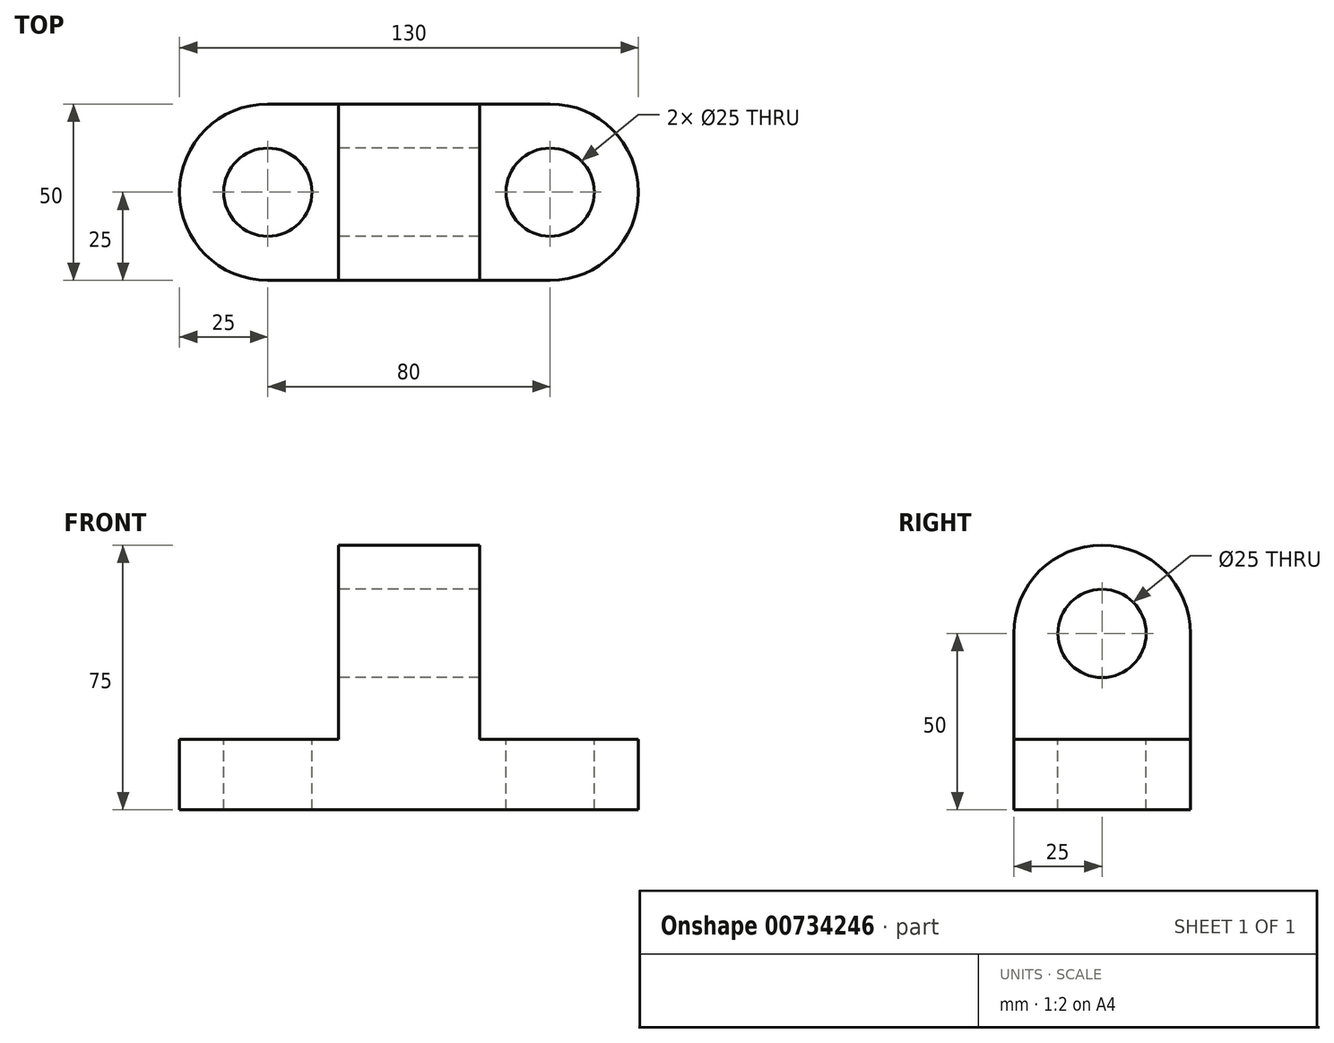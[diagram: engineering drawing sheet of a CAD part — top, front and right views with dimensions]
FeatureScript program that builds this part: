
annotation { "Feature Type Name" : "Feature", "Feature Type Description" : "" }
export const myFeature = defineFeature(function(context is Context, id is Id, definition is map)
    precondition{}
    {
        {
            var Q0;
            Q0=qCreatedBy(makeId("Top.planeOp"),FACE);
            var sketch = newSketch(context, id + "F0", { "sketchPlane" : qUnion([Q0])});
            skLineSegment(sketch, "E0", {"start": v(0, 50) * mm, "end": v(80, 50) * mm});
            skLineSegment(sketch, "E1", {"start": v(0, 0) * mm, "end": v(80, 0) * mm});
            skArc(sketch, "E2", {"start": v(80, 0) * mm, "mid": v(105, 25) * mm, "end": v(80, 50) * mm});
            skArc(sketch, "E3", {"start": v(0, 50) * mm, "mid": v(-25, 25) * mm, "end": v(0, 0) * mm});
            skSolve(sketch);
        }
        {
            var Q0;
            Q0=makeQuery(id+"F0.imprint","IMPRINT",FACE,{"disambiguationData":[TD([[makeQuery(id+"F0.imprint","IMPRINT",EDGE,{"derivedFrom":sQuery(id+"F0.wireOp",EDGE,"E0")}),-1.0]])]});
            extrude(context, id + "F1", {"entities" : qUnion([Q0]), "depth" : 20 * mm, "offsetDistance" : 25 * mm});
        }
        {
            var Q0;
            Q0=makeQuery(id+"F1.opExtrude","CAP_FACE",FACE,{"disambiguationData":[OSD([sQuery(id+"F0.wireOp",EDGE,"E0"),sQuery(id+"F0.wireOp",EDGE,"E1"),sQuery(id+"F0.wireOp",EDGE,"E2"),sQuery(id+"F0.wireOp",EDGE,"E3")])],"isStart":false});
            var sketch = newSketch(context, id + "F2", { "sketchPlane" : qUnion([Q0])});
            skLineSegment(sketch, "E4", {"start": v(20, 50) * mm, "end": v(20, 0) * mm});
            skLineSegment(sketch, "E5", {"start": v(60, 50) * mm, "end": v(60, 0) * mm});
            skSolve(sketch);
        }
        {
            var Q0;
            {var subQ0=sQuery(id+"F2.wireOp",EDGE,"E4");Q0=makeQuery(id+"F2.imprint","IMPRINT",FACE,{"disambiguationData":[TD([[makeQuery(id+"F2.imprint","IMPRINT",EDGE,{"derivedFrom":subQ0}),1.0]])]});}
            extrude(context, id + "F3", {"entities" : qUnion([Q0]), "operationType" : NewBodyOperationType.ADD, "depth" : 30 * mm, "offsetDistance" : 25 * mm});
        }
        {
            var Q0;
            Q0=makeQuery(id+"F3.opExtrude","SWEPT_FACE",FACE,{"disambiguationData":[OSD([sQuery(id+"F2.wireOp",EDGE,"E5")])]});
            var sketch = newSketch(context, id + "F4", { "sketchPlane" : qUnion([Q0])});
            skArc(sketch, "E6", {"start": v(50, 50) * mm, "mid": v(25, 75) * mm, "end": v(0, 50) * mm});
            skLineSegment(sketch, "E7.0", {"start": v(0, 20) * mm, "end": v(50, 20) * mm});
            skSolve(sketch);
        }
        {
            var Q0;
            Q0=makeQuery(id+"F4.imprint","IMPRINT",FACE,{"disambiguationData":[TD([[makeQuery(id+"F4.imprint","IMPRINT",EDGE,{"derivedFrom":sQuery(id+"F4.wireOp",EDGE,"E6")}),1.0]])]});
            var Q1;
            Q1=makeQuery(id+"F3.opExtrude","SWEPT_FACE",FACE,{"disambiguationData":[OSD([sQuery(id+"F2.wireOp",EDGE,"E4")])]});
            extrude(context, id + "F5", {"entities" : qUnion([Q0]), "operationType" : NewBodyOperationType.ADD, "endBound" : BoundingType.UP_TO_SURFACE, "oppositeDirection" : true, "depth" : 25 * mm, "endBoundEntityFace" : qUnion([Q1]), "offsetDistance" : 25 * mm});
        }
        {
            var Q0;
            {var subQ0=sQuery(id+"F2.wireOp",EDGE,"E4");Q0=makeQuery(id+"F5.boolean.opBoolean","MERGE",FACE,{"derivedFrom":[makeQuery(id+"F3.opExtrude","SWEPT_FACE",FACE,{"disambiguationData":[OSD([subQ0])]}),makeQuery(id+"F5.opExtrude","CAP_FACE",FACE,{"disambiguationData":[OSD([subQ0])],"isStart":false})]});}
            var sketch = newSketch(context, id + "F6", { "sketchPlane" : qUnion([Q0])});
            skCircle(sketch, "E8", {"center": v(-25, 50) * mm, "radius": 12.5 * mm});
            skSolve(sketch);
        }
        {
            var Q0;
            Q0=makeQuery(id+"F6.imprint","IMPRINT",FACE,{"disambiguationData":[TD([[makeQuery(id+"F6.imprint","IMPRINT",EDGE,{"derivedFrom":sQuery(id+"F6.wireOp",EDGE,"E8")}),1.0]])]});
            var Q1;
            {var subQ0=sQuery(id+"F2.wireOp",EDGE,"E5");Q1=makeQuery(id+"F5.boolean.opBoolean","MERGE",FACE,{"derivedFrom":[makeQuery(id+"F3.opExtrude","SWEPT_FACE",FACE,{"disambiguationData":[OSD([subQ0])]}),makeQuery(id+"F5.opExtrude","CAP_FACE",FACE,{"disambiguationData":[OSD([subQ0,sQuery(id+"F4.wireOp",EDGE,"E6")])],"isStart":true})]});}
            extrude(context, id + "F7", {"entities" : qUnion([Q0]), "operationType" : NewBodyOperationType.REMOVE, "endBound" : BoundingType.UP_TO_SURFACE, "oppositeDirection" : true, "depth" : 25 * mm, "endBoundEntityFace" : qUnion([Q1]), "offsetDistance" : 25 * mm});
        }
        {
            var Q0;
            {var subQ0=sQuery(id+"F0.wireOp",EDGE,"E2");var subQ1=sQuery(id+"F0.wireOp",EDGE,"E1");var subQ2=sQuery(id+"F0.wireOp",EDGE,"E0");Q0=makeQuery(id+"F3.boolean.opBoolean","SPLIT",FACE,{"disambiguationData":[TD([makeQuery(id+"F1.opExtrude","SWEPT_FACE",FACE,{"disambiguationData":[OSD([subQ0])]})])],"derivedFrom":makeQuery(id+"F1.opExtrude","CAP_FACE",FACE,{"disambiguationData":[OSD([subQ2,subQ1,subQ0,sQuery(id+"F0.wireOp",EDGE,"E3")])],"isStart":false})});}
            var sketch = newSketch(context, id + "F8", { "sketchPlane" : qUnion([Q0])});
            skCircle(sketch, "E9", {"center": v(80, 25) * mm, "radius": 12.5 * mm});
            skCircle(sketch, "E10", {"center": v(0, 25) * mm, "radius": 12.5 * mm});
            skSolve(sketch);
        }
        {
            var Q0;
            Q0=makeQuery(id+"F8.imprint","IMPRINT",FACE,{"disambiguationData":[TD([[makeQuery(id+"F8.imprint","IMPRINT",EDGE,{"derivedFrom":sQuery(id+"F8.wireOp",EDGE,"E10")}),1.0]])]});
            var Q1;
            Q1=makeQuery(id+"F8.imprint","IMPRINT",FACE,{"disambiguationData":[TD([[makeQuery(id+"F8.imprint","IMPRINT",EDGE,{"derivedFrom":sQuery(id+"F8.wireOp",EDGE,"E9")}),1.0]])]});
            var Q2;
            Q2=makeQuery(id+"F1.opExtrude","CAP_FACE",FACE,{"disambiguationData":[OSD([sQuery(id+"F0.wireOp",EDGE,"E0"),sQuery(id+"F0.wireOp",EDGE,"E1"),sQuery(id+"F0.wireOp",EDGE,"E2"),sQuery(id+"F0.wireOp",EDGE,"E3")])],"isStart":true});
            extrude(context, id + "F9", {"entities" : qUnion([Q0, Q1]), "operationType" : NewBodyOperationType.REMOVE, "endBound" : BoundingType.UP_TO_SURFACE, "oppositeDirection" : true, "depth" : 25 * mm, "endBoundEntityFace" : qUnion([Q2]), "offsetDistance" : 25 * mm});
        }
    });
